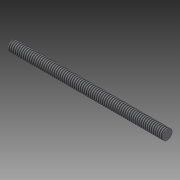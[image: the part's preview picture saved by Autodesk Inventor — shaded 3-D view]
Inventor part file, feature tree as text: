
AUTODESK INVENTOR PART (.ipt)
format: ipt  version: 2015 (Build 190159000, 159)  size: 73,728 bytes
history: native  units: in
note: dims shown in document units (in); Inventor stores cm internally (conversion verified against a paired STEP export)
features: extrude x1, thread x1, sketch x1
ambient origin geometry x8: Origin, YZ Plane, XZ Plane, XY Plane, X Axis, Y Axis, Z Axis, Center Point
bodies: Solid1 (feature_tree)
feature tree (3):
  extrude  "Extrusion1"  Depth=6.0in TaperAngle=0.0deg
  thread  "Thread1"  [1 undecoded]
  sketch  "Sketch1"  dims[d0=0.3937in d1=6.0in d2=0.0in d3=1.0in d4=0.0in]
note: 1 required parameter value undecoded (feature->parameter linkage not recoverable at this tier; creation-order binding heuristic only, values carry confidence <= 0.55)
